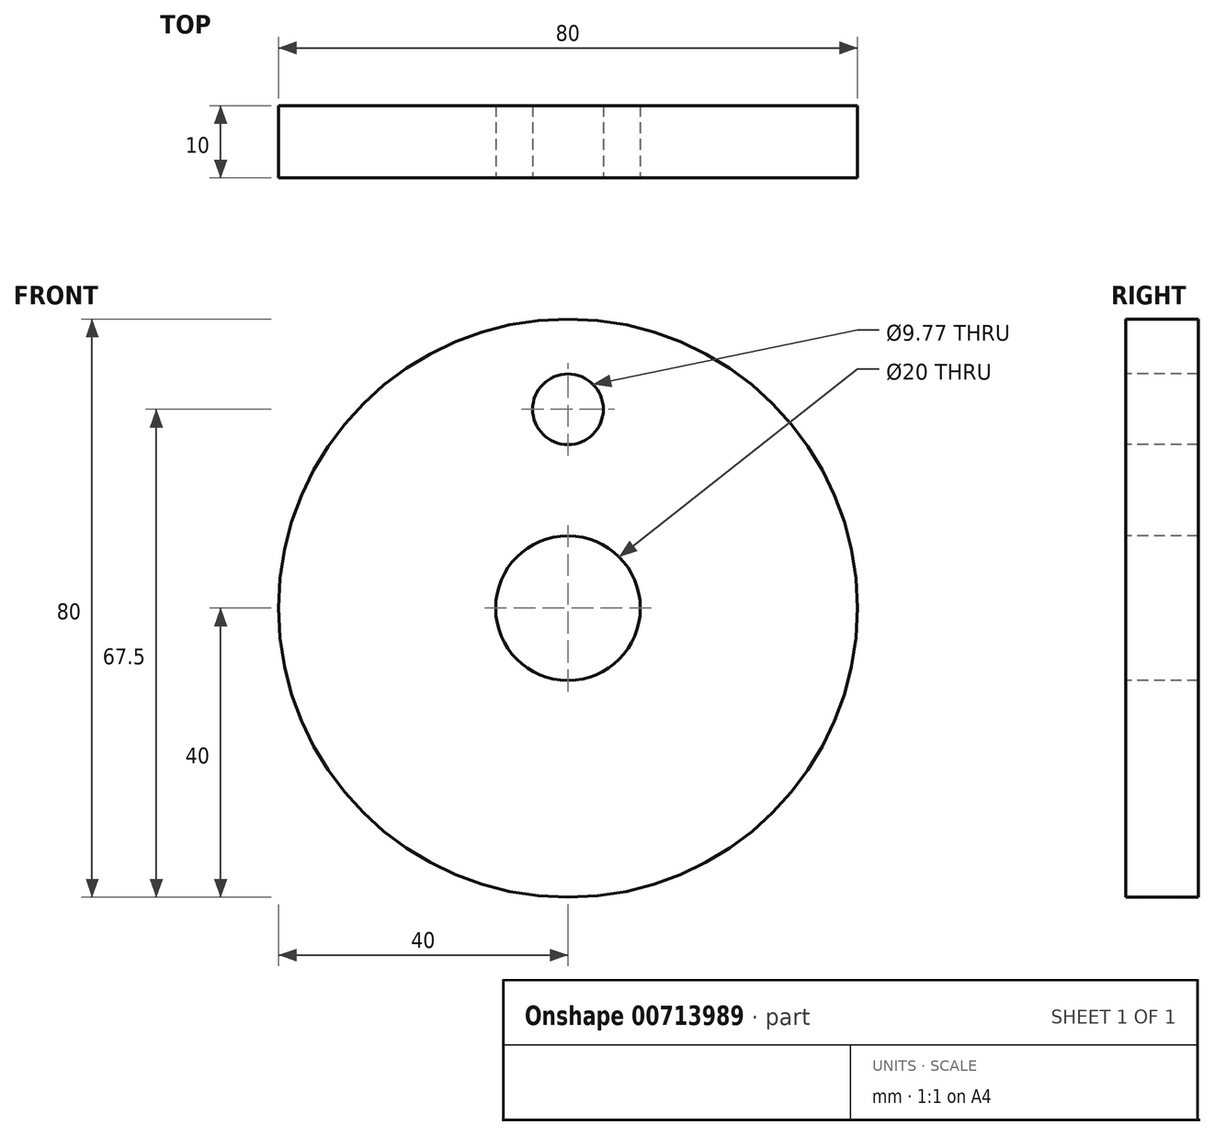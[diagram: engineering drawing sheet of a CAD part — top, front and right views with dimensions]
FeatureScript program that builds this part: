
annotation { "Feature Type Name" : "Feature", "Feature Type Description" : "" }
export const myFeature = defineFeature(function(context is Context, id is Id, definition is map)
    precondition{}
    {
        {
            var Q0;
            Q0=qCreatedBy(makeId("Front.planeOp"),FACE);
            var sketch = newSketch(context, id + "F0", { "sketchPlane" : qUnion([Q0])});
            skCircle(sketch, "E0", {"center": v(0, 0) * mm, "radius": 40 * mm});
            skSolve(sketch);
        }
        {
            var Q0;
            Q0=qSketchRegion(id+"F0",true);
            extrude(context, id + "F1", {"entities" : qUnion([Q0]), "depth" : 10 * mm});
        }
        {
            var Q0;
            Q0=makeQuery(id+"F1.opExtrude","CAP_FACE",FACE,{"disambiguationData":[OSD([sQuery(id+"F0.wireOp",EDGE,"E0")])],"isStart":false});
            var sketch = newSketch(context, id + "F2", { "sketchPlane" : qUnion([Q0])});
            skCircle(sketch, "E1", {"center": v(0, 0) * mm, "radius": 27.5 * mm, "construction": true});
            skCircle(sketch, "E2", {"center": v(0, 27.5) * mm, "radius": 4.89 * mm});
            skSolve(sketch);
        }
        {
            var Q0;
            Q0=qSketchRegion(id+"F2",true);
            extrude(context, id + "F3", {"entities" : qUnion([Q0]), "operationType" : NewBodyOperationType.REMOVE, "oppositeDirection" : true, "depth" : 25 * mm});
        }
        {
            var Q0;
            Q0=makeQuery(id+"F1.opExtrude","CAP_FACE",FACE,{"disambiguationData":[OSD([sQuery(id+"F0.wireOp",EDGE,"E0")])],"isStart":false});
            var sketch = newSketch(context, id + "F4", { "sketchPlane" : qUnion([Q0])});
            skCircle(sketch, "E3", {"center": v(0, 0) * mm, "radius": 10 * mm});
            skSolve(sketch);
        }
        {
            var Q0;
            Q0=qSketchRegion(id+"F4",true);
            extrude(context, id + "F5", {"entities" : qUnion([Q0]), "operationType" : NewBodyOperationType.REMOVE, "oppositeDirection" : true, "depth" : 25 * mm});
        }
    });
